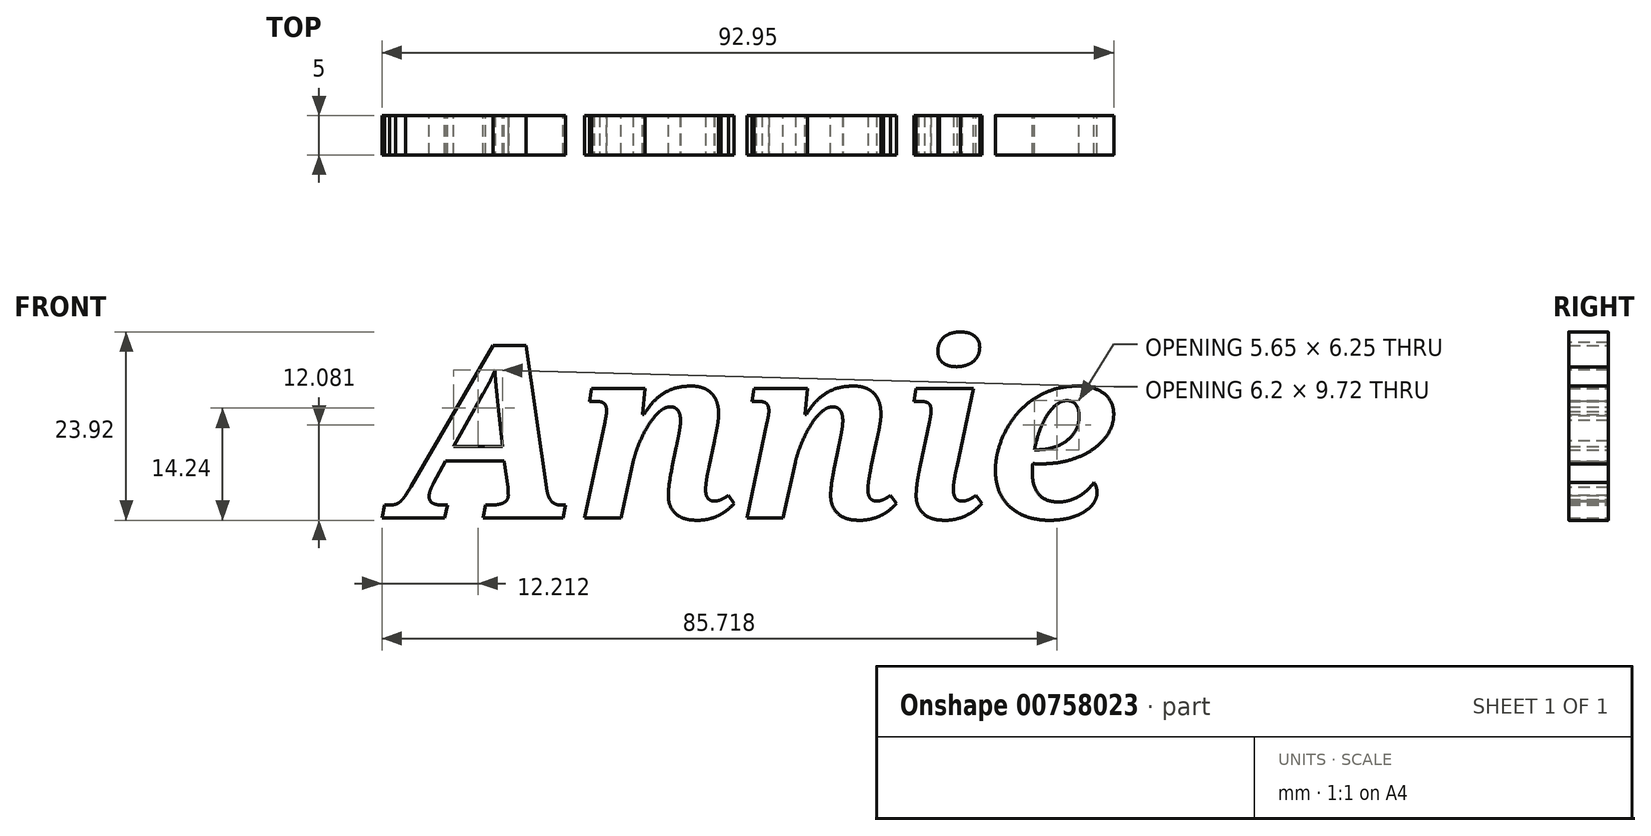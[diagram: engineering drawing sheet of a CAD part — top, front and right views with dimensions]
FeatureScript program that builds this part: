
annotation { "Feature Type Name" : "Feature", "Feature Type Description" : "" }
export const myFeature = defineFeature(function(context is Context, id is Id, definition is map)
    precondition{}
    {
        {
            var Q0;
            Q0=qCreatedBy(makeId("Front.planeOp"),FACE);
            var sketch = newSketch(context, id + "F0", { "sketchPlane" : qUnion([Q0])});
            skText(sketch, "E0", { "text": "Annie", "fontName": "NotoSerif-BoldItalic.ttf"});
            const initialGuessF0  = {"E0": [-0.04735, 0.01188, 1, 0, 0.02209]};
            skSetInitialGuess(sketch, initialGuessF0);
            skSolve(sketch);
        }
        {
            var Q0;
            Q0 = qSketchRegion(id + "F0", true);
            extrude(context, id + "F1", {"entities" : qUnion([Q0]), "depth" : 5 * mm, "offsetDistance" : 25 * mm});
        }
    });
